# Revit family: prevedo_ILUMAG
name_source: partatom
category: Leuchten
revit_build: Autodesk Revit 2018 (Build: 20190510_1515(x64)
units: mm (PartAtom-declared; Revit-internal decimal feet)

## family parameters
Basisbauteil = Fläche
Beim Laden mit Abzugskörper schneiden = Ja
Bemaßung runder Anschluss = Durchmesser verwenden
Gemeinsam genutzt = Nein
Lichtquelle = Ja
OmniClass-Nummer = 23.80.70.00
OmniClass-Titel = Lighting
Raumberechnungspunkt = Nein
Teiletyp = Normal

## types (5) — shared parameters
12 Volt = Ja
24 Volt = Nein
Ausbildung Leuchtmittel = LED
Ausführungsunterlagen = gemäß Zeichnung und Einzelbeschreibung
Bauelement = Leuchte
Bauteil, Leuchte/Lampe = Anbauleuchte
Befestigung Leuchte = Direktes Aufbringen auf die Wand möglich. Optional ist ein Aufhängerahmen verfügbar, der auch das Unterbringen eines Trafos ermöglicht.
Dimmbarkeit Leuchte = elektronisch dimmbar
Emissionsform beim Rendern sichtbar = Nein
Energieeffizienzklasse = A+
Farbfilter = 16777215
Farbtemperaturverschiebung bei Dämpfen der Lampe = <Keine Auswahl>
Größe des Lichtquellensymbols = 50 mm  [stored 0.164042 ft]
Hersteller = prevedo Lichtmedien GmbH
Intensität = 800 lm/m²
Lampe = LED
Lebensdauer h Leuchtmittel = mind. 50000
Leuchte Bauweise = Abdeckscheibe aus Kunststoff
Material Abdeckung = Kunststoff_leuchtend
Produktinformationen = https://www.prevedo.de
Schaltungsweise = Betriebsgerät elektronisch
Spannung = 12 V
Typenkommentare = Bei 230V Zuleitung ist ein Trafo notwendig. Dieser und weiteres Zubehör ist separat erhältlich.
URL = https://www.prevedo.de
Umgebungstemperatur = -15°C bis +40°C
Variante Einbau = Nein
Vorgabe-Ansicht = 1219 mm
Werkstoff, Gehäuse = Stahl, nichtrostend
zB01_max = 1200 mm
zL01_min = 150 mm
zero-valued in all types: B_Versatz Einfügepos, B_check_error

## per-type parameters (varying)
| type | Anwendung | B_Rahmen Dicke l/r | B_Rahmen Dicke o/u | Beschreibung | Breite | Dicke (nicht editierbar) | Gewicht | Laenge | Leistung W Leuchtmittel | Scheinlast | Schutzart | Von Breite des Rechtecks ausssenden | Von Länge des Rechtecks aussenden | zB01 | zB01_min | zD01 | zL01 | zL01_max |
| ILUMAG tile | Als wassergeschützte, sehr flache Leuchtbildfliese mit wechselbaren Backlit-Motiven erschließt ILUMAG tile ganz neue Gestaltungsmöglichkeiten für Feuchträume wie Bäder, Duschen oder Küchen. Dabei gibt es sowohl Anwendungen im privaten Bereich mit Schwerpunkt Dekoration als auch im öffentlichen Bereich, z.B. für die Information in Schwimmbädern oder Saunen. | 25 mm  [stored 0.082021 ft] | 25 mm  [stored 0.082021 ft] | Die Bauhöhe von nur 6 mm erlaubt den Einsatz der Leuchtbildfliese in jedem herkömmlichen Keramik-Fliesenspiegel nach Kundenwunsch im Format bis ca. 1 x 2 m. Sie kann sowohl beim Neubau als auch für die Nachrüstung einer Wand eingesetzt werden. Die nötige 12/24 V-Stromzufuhr erfolgt üblich mit einem in einer Fuge versteckten Kabel und einer hinter der Leuchtbildfliese in einer Vertiefung verbauten Anschlussklemme, so dass auch eine ggf. nötige Reparatur unkompliziert ist. Der Bildwechsel ist elegant analog dem ILUMAG flex dank der Haftkleber-Beschichtung ausführbar. | 300 mm | 6 mm  [stored 0.019685 ft] | ca. 9kg/m² | 900 mm  [stored 2.95276 ft] | 16 W | 16 VA | spritzwassergeschützt, angenähert an IP65 | 250 mm  [stored 0.82021 ft] | 850 mm  [stored 2.78871 ft] | 300 mm | 150 mm | 6 mm  [stored 0.019685 ft] | 900 mm  [stored 2.95276 ft] | 2000 mm  [stored 6.56168 ft] |
| ILUMAG flex | Dies ist unsere neuartige Lösung für leicht wechselbare Motive. Überall, wo es auf eine starke Präsentation mit Licht ankommt – in Foyers, in Beratungsräumen, in Shops, bei Messeauftritten und vielem mehr – überzeugt ILUMAG flex mit Qualität, Eleganz und leichtem Bildwechsel bei niedrigen Kosten. Mit der Reduzierung auf das Wesentliche ist ILUMAG flex die ideale "Spielwiese" für Kreative und eine echte Alternative bzw. Ergänzung zu digitalen Systemen. | 20 mm  [stored 0.0656168 ft] | 5 mm  [stored 0.0164042 ft] | Grundaufbau und Abmaße gleichen denen von ILUMAG perm. Ergänzt wird ILUMAG flex durch eine Deckscheibe mit Haftkleber-Beschichtung. Diese erlaubt den leichten und ständig wiederholbaren Wechsel von üblichen, preiswerten Backlitfolien (mit oder ohne Schutzlaminat). Damit liegt die Bauhöhe bei max. 8 mm. Auf Wunsch wird das System rückseitig mit Rahmen oder Leisten zum Aufhängen (längs oder quer) geliefert. Für einen kaum sichtbaren Stromanschluss kann ein selbstklebendes, überstreichbares Flachkabel benutzt werden. | 600 mm | 6 mm  [stored 0.019685 ft] | ca. 9kg/m² | 1400 mm  [stored 4.59318 ft] | 24 W | 24 VA | staubgeschützt, angenähert an IP22 | 550 mm | 1350 mm  [stored 4.42913 ft] | 600 mm | 150 mm | 6 mm  [stored 0.019685 ft] | 1400 mm  [stored 4.59318 ft] | 2000 mm  [stored 6.56168 ft] |
| ILUMAG perm | ILUMAG perm bietet sich als preiswerte Lösung überall dort an , wo ein einfaches, platzsparendes Leuchtmodul mit permantem Motiv gebraucht wird, wie z.B. im Badbereich in einer Nische, im Verkauf am POS oder im gewerblichen Umfeld zur Information mit Licht | 20 mm  [stored 0.0656168 ft] | 5 mm  [stored 0.0164042 ft] | Mit einer Gesamthöhe von 5 mm und einer Maximalgröße von 120 x 200 cm kann das LED-Panel mit Alu-Rückwand für permanente Backlit-Motive (ggf. mit rückseitigem Aufhängerahmen) vielfältig eingesetzt werden. An zwei Seiten hat es eine fast rahmenlose Optik. Dadurch kann ein großes Bild ggf. gut paneliert werden. Auf der Sichtfläche wird üblicherweise ein Backlit, oft mit mattem Schutzlaminat (Motiv entspiegelt), verklebt. | 1000 mm  [stored 3.28084 ft] | 6 mm  [stored 0.019685 ft] | ca. 8kg/m² | 1000 mm  [stored 3.28084 ft] | 40 W | 40 VA | staubgeschützt, angenähert an IP22 | 950 mm  [stored 3.1168 ft] | 950 mm  [stored 3.1168 ft] | 1000 mm  [stored 3.28084 ft] | 150 mm | 6 mm  [stored 0.019685 ft] | 1000 mm  [stored 3.28084 ft] | 2000 mm  [stored 6.56168 ft] |
| ILUMAG top | Ob z.B. in Kunst-Galerien, im Shopping-Bereich oder zur Information in großen Gebäuden – ILUMAG top erfüllt mit seiner eleganten Erscheinung und seiner guten Funktionalität höchste Ansprüche brillanter Präsentation und variabler Raumgestaltung. Viele Aufgaben der Innenarchitektur können mit diesem wechselbaren System gelöst werden. Mit ihm ist es ein Leichtes, Ausstellungen oder Räumen den aktuell gewünschten Charakter zu geben. ILUMAG top bringt mit seinem angenehmen Licht Kunstwerke zum Strahlen und Flair in jede Begegnungstätte. | 20 mm  [stored 0.0656168 ft] | 5 mm  [stored 0.0164042 ft] | ILUMAG top hat vergleichbare Abmaße und Funktionalitäten wie ILUMAG flex. Der wesentliche Unterschied ist die Abdeckung der einzulegenden Backlit-Folie mit einer hochwertigen Acryl-Scheibe. Diese besitzt eine gehärteten Oberfläche (matt oder glänzend). Sie wird mit einem speziellen Magnet-System, verdeckt durch 25 mm-Metallstreifen, verschlossen. ILUMAG top kann dank zweier rahmenloser Kanten auch zum Darstellen übergroßer Bilder durch Panelierung eingesetzt werden. Das System wird nach Bedarf mit passendem Zubehör für eine einfache Montage (quer oder längs) mit 10 mm-Wandabstand geliefert. | 500 mm  [stored 1.64042 ft] | 9 mm  [stored 0.0295276 ft] | ca. 9kg/m² | 1200 mm | 24 W | 24 VA | staubgeschützt, angenähert an IP22 | 450 mm  [stored 1.47638 ft] | 1150 mm | 500 mm  [stored 1.64042 ft] | 150 mm | 9 mm  [stored 0.0295276 ft] | 1200 mm | 2000 mm  [stored 6.56168 ft] |
| ILUMAG splash | Dieses wetterfeste Leuchtschild mit einer frei gestaltbaren Sichtfläche hat sein Einsatzfeld im Außenbereich - u.a. an Hausfassaden, an Aufstellern oder Dachkonstruktionen. Aber auch im Innenbereich, wo hohe Anforderungen an den Spritzwasserschutz bestehen, ist es durch seine flache Bauweise oftmals eine optimale Lösung. Dies betrifft insbesondere großformatige Leuchtflächen in Feuchträumen wie Duschrückwände oder typische Bad- oder Sauna-Bilder. | 20 mm  [stored 0.0656168 ft] | 5 mm  [stored 0.0164042 ft] | Als voll abgedichteter Leuchtkasten mit nur 23 mm Tiefe bietet ILUMAG billboard bei einer Leuchtfläche von bis zu 1,2 x 2,5 m die hier nötige hohe Stabilität. Außerdem kann die Sichtfläche je nach Bedarf mit einem wechselbaren Motiv auf transluzenter Backlitfolie bespielt werden. Er setzt bezüglich Energieeffizienz Maßstäbe und besticht im Vergleich mit Leuchtkästen anderer Bauart in diesem Bereich durch seine Eleganz sowie Variabilität. | 1000 mm  [stored 3.28084 ft] | 23 mm  [stored 0.0754593 ft] | ca. 25kg/m² | 2000 mm  [stored 6.56168 ft] | 40 W | 40 VA | spritzwassergeschützt, angenähert an IP65 | 950 mm  [stored 3.1168 ft] | 1950 mm  [stored 6.39764 ft] | 1000 mm  [stored 3.28084 ft] | 200 mm  [stored 0.656168 ft] | 23 mm  [stored 0.0754593 ft] | 2000 mm  [stored 6.56168 ft] | 2500 mm  [stored 8.2021 ft] |

note: column(s) folded — value = type name in every type: Modell

note: [stored X ft] marks values corroborated as IEEE doubles in the binary element streams (Revit-internal decimal feet)
